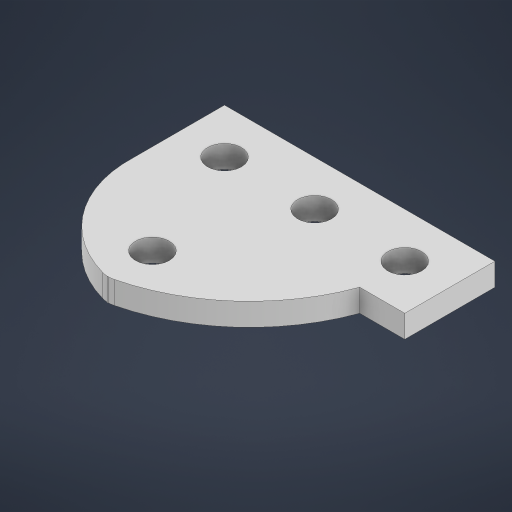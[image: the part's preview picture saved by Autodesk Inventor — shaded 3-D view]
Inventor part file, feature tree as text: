
AUTODESK INVENTOR PART (.ipt)
format: ipt  version: 2024 (Build 280153000, 153)  size: 226,304 bytes
history: native  units: in
note: dims shown in document units (in); Inventor stores cm internally (conversion verified against a paired STEP export)
features: sketch x1, extrude x1, hole x1
ambient origin geometry x8: Origin, YZ Plane, XZ Plane, XY Plane, X Axis, Y Axis, Z Axis, Center Point
bodies: Solid1 (feature_tree)
feature tree (3):
  sketch  "Sketch1"  dims[d0=1.5in d1=0.5in d2=0.5in d3=0.5in d4=0.4in d6=0.5in d7=0.25in d8=0.125in d9=0.0in d13=0.1875in d14=0.75in d15=0.375in d16=0.25in d17=0.5635in d18=1.0in d19=0.8108in d20=0.125in]
  extrude  "Extrusion1"  Depth=0.5in
  hole  "Hole1"  [1 undecoded]
note: 1 required parameter value undecoded (feature->parameter linkage not recoverable at this tier; creation-order binding heuristic only, values carry confidence <= 0.55)
